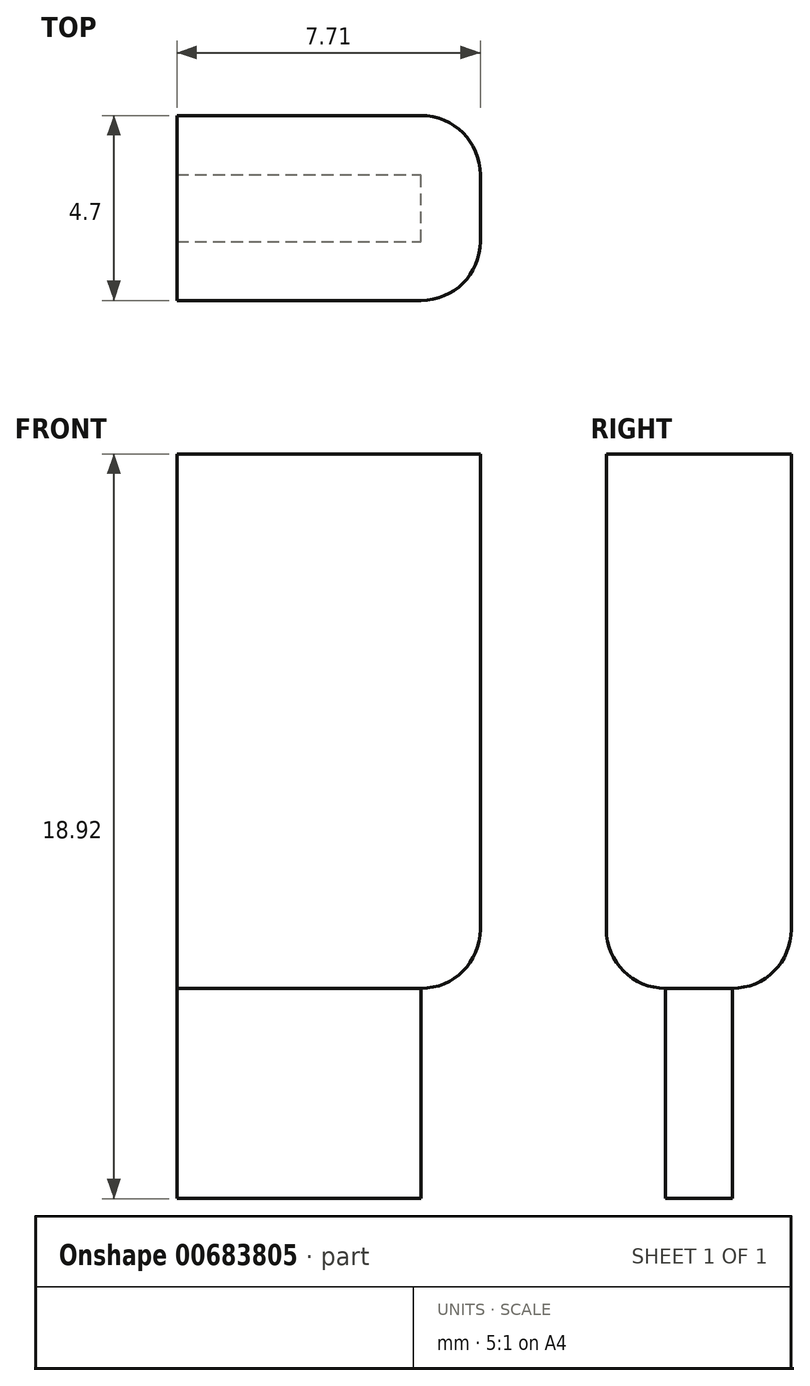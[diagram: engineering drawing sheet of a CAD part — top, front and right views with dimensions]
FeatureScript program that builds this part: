
annotation { "Feature Type Name" : "Feature", "Feature Type Description" : "" }
export const myFeature = defineFeature(function(context is Context, id is Id, definition is map)
    precondition{}
    {
        {
            var Q0;
            Q0=qCreatedBy(makeId("Front.planeOp"),FACE);
            var sketch = newSketch(context, id + "F0", { "sketchPlane" : qUnion([Q0])});
            skLineSegment(sketch, "E0.bottom", {"start": v(-29.2, 31.71) * mm, "end": v(-21.43, 31.71) * mm});
            skLineSegment(sketch, "E0.top", {"start": v(-29.2, 45.3) * mm, "end": v(-21.43, 45.3) * mm});
            skLineSegment(sketch, "E0.left", {"start": v(-29.2, 31.71) * mm, "end": v(-29.2, 45.3) * mm});
            skLineSegment(sketch, "E0.right", {"start": v(-21.43, 31.71) * mm, "end": v(-21.43, 45.3) * mm});
            skSolve(sketch);
        }
        {
            var Q0;
            Q0=makeQuery(id+"F0.imprint","IMPRINT",FACE,{"disambiguationData":[TD([[makeQuery(id+"F0.imprint","IMPRINT",EDGE,{"derivedFrom":sQuery(id+"F0.wireOp",EDGE,"E0.bottom")}),1.0]])]});
            extrude(context, id + "F1", {"entities" : qUnion([Q0]), "depth" : 4.7 * mm, "offsetDistance" : 25 * mm});
        }
        {
            var Q0;
            Q0=makeQuery(id+"F1.opExtrude","SWEPT_FACE",FACE,{"disambiguationData":[OSD([sQuery(id+"F0.wireOp",EDGE,"E0.left")])]});
            extrude(context, id + "F2", {"entities" : qUnion([Q0]), "operationType" : NewBodyOperationType.REMOVE, "oppositeDirection" : true, "depth" : 0.05 * mm, "offsetDistance" : 25 * mm});
        }
        {
            var Q0;
            {var subQ0=sQuery(id+"F0.wireOp",EDGE,"E0.left");Q0=makeQuery(id+"F2.boolean.opBoolean","COPY",EDGE,{"derivedFrom":makeQuery(id+"F2.opExtrude","CAP_EDGE",EDGE,{"disambiguationData":[OSD([subQ0]),TDD([makeQuery(id+"F1.opExtrude","CAP_EDGE",EDGE,{"disambiguationData":[OSD([subQ0])],"isStart":false})])],"isStart":false})});}
            var Q1;
            {var subQ0=sQuery(id+"F0.wireOp",EDGE,"E0.left");Q1=makeQuery(id+"F2.boolean.opBoolean","COPY",EDGE,{"derivedFrom":makeQuery(id+"F2.opExtrude","CAP_EDGE",EDGE,{"disambiguationData":[OSD([subQ0]),TDD([makeQuery(id+"F1.opExtrude","CAP_EDGE",EDGE,{"disambiguationData":[OSD([subQ0])],"isStart":true})])],"isStart":false})});}
            var Q2;
            Q2=makeQuery(id+"F1.opExtrude","CAP_EDGE",EDGE,{"disambiguationData":[OSD([sQuery(id+"F0.wireOp",EDGE,"E0.right")])],"isStart":true});
            var Q3;
            Q3=makeQuery(id+"F1.opExtrude","CAP_EDGE",EDGE,{"disambiguationData":[OSD([sQuery(id+"F0.wireOp",EDGE,"E0.right")])],"isStart":false});
            var Q4;
            Q4=makeQuery(id+"F1.opExtrude","CAP_EDGE",EDGE,{"disambiguationData":[OSD([sQuery(id+"F0.wireOp",EDGE,"E0.bottom")])],"isStart":false});
            var Q5;
            Q5=makeQuery(id+"F1.opExtrude","CAP_EDGE",EDGE,{"disambiguationData":[OSD([sQuery(id+"F0.wireOp",EDGE,"E0.bottom")])],"isStart":true});
            var Q6;
            Q6=makeQuery(id+"F1.opExtrude","SWEPT_EDGE",EDGE,{"disambiguationData":[OSD([sQuery(id+"F0.wireOp",EDGE,"E0.bottom"),sQuery(id+"F0.wireOp",EDGE,"E0.right")])]});
            var Q7;
            Q7=makeQuery(id+"F2.boolean.opBoolean","COPY",EDGE,{"derivedFrom":makeQuery(id+"F2.opExtrude","CAP_EDGE",EDGE,{"disambiguationData":[OSD([sQuery(id+"F0.wireOp",EDGE,"E0.bottom"),sQuery(id+"F0.wireOp",EDGE,"E0.left")])],"isStart":false})});
            fillet(context, id + "F3", {"entities" : qUnion([Q0, Q1, Q2, Q3, Q4, Q5, Q6, Q7]), "radius" : 1.5 * mm, "tangentPropagation" : true, "allowEdgeOverflow" : false});
        }
        {
            var Q0;
            Q0=makeQuery(id+"F1.opExtrude","SWEPT_FACE",FACE,{"disambiguationData":[OSD([sQuery(id+"F0.wireOp",EDGE,"E0.bottom")])]});
            extrude(context, id + "F4", {"entities" : qUnion([Q0]), "operationType" : NewBodyOperationType.ADD, "depth" : 5.34 * mm, "offsetDistance" : 25 * mm});
        }
    });
